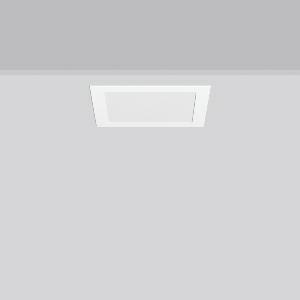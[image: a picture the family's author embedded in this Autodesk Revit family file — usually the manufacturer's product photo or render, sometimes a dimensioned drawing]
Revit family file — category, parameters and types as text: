
# Revit family: toledo_flat_square_e_672243_002_1_89_9464
name_source: partatom
category: Lighting Fixtures
units: mm (PartAtom-declared; Revit-internal decimal feet)

## family parameters
Cut with Voids When Loaded = No
Host = Face
Light Source = No
Part Type = Normal
Room Calculation Point = No
Round Connector Dimension = Use Diameter
Shared = No

## types (1)
- TOLEDO FLAT square E (1 x LED Modul 840, 1650 lm, 4000)
    Apparent Load = 19 VA
    CIE Flux Codes = 49 80 96 100 100
    Color Rendering = 80
    Color Temperature = 4000
    Default Elevation = 1800 mm
    Description = Series: TOLEDO FLAT square
Square recessed downlight. For escape route illumination. Housing: die-cast aluminium, powder-coated. Lightguide and diffuser made of non-yellowing plastic (PMMA). Diffuser opal matt plastic. Ceiling installation with spring system. Including separate LED converter with connecting cable 250 mm. Suitable for connection to central battery systems. With AC Control monitoring module for LUXIFAIR central battery units. External driver with simple plug-in locking system. 
Colour: white
Length: 225 mm
Width: 225 mm
Height: 3 mm
Cut-out length: 208 mm
Cut-out width: 208 mm
Recess height: 40 mm
Luminaire: recess height: 37-57 mm
Weight: 1.47 kg
Operating mode: maintained power mode
Lamp: LED
Socket: without socket
Colour temperature: 4000K
Colour rendering index (CRI): 80
System power: 19 W
Rated luminous flux: 1650 lm
Luminous flux, emergency: 1650 lm
System power, emergency: 19 W
Control gear: Regulated power supply
Protection class: I
Type of protection: IP 54
    Height = 0 mm  [stored 0 ft]
    Lamp = 1 x LED Modul 840
    Lamp Light Flux = 1650 lm
    Lamp count = 1
    Length = 225 mm
    Lifetime = 50000 h
    Luminous efficacy = 87 lm/W
    Manufacturer = RZB
    ModVariant = No
    Model = 672243.002.1.89
    Mounting Place = Ceiling
    Mounting Type = Recessed
    Number of Poles = 1
    OnlyDefault = Yes
    Power Factor = 1
    Product Name = TOLEDO FLAT square E
    Product group = Recessed downlights
    ProductGroupID = 402
    Protection Class = Protection class I
    Protection Degree = IP 40
    RLX_Detail_Level = 1
    RLX_Emergency_Light_Flux = 1650 lm
    RLX_Emergency_Type = 3
    RLX_Emergency_Type_DB = Yes
    RlxData = <blob elided: 11057 chars, md5=1d8146d6>
    Socket = socket
    Standby Power = 0 W
    System Light Flux = 1650 lm
    System Power = 19 W
    Type Comments = Product without accessories
    Type Image = 901487.002.jpg
    URL = http://relux.com
    VarID = ---
    Voltage = 230 V
    Voltage Range = 220-240 V
    Weight = 0.00 kg
    Width = 225 mm

note: [stored X ft] marks values corroborated as IEEE doubles in the binary element streams (Revit-internal decimal feet)

## geometry (parser evidence)
native form markers: Sweep x9
no freeform markers — native parametric forms only
